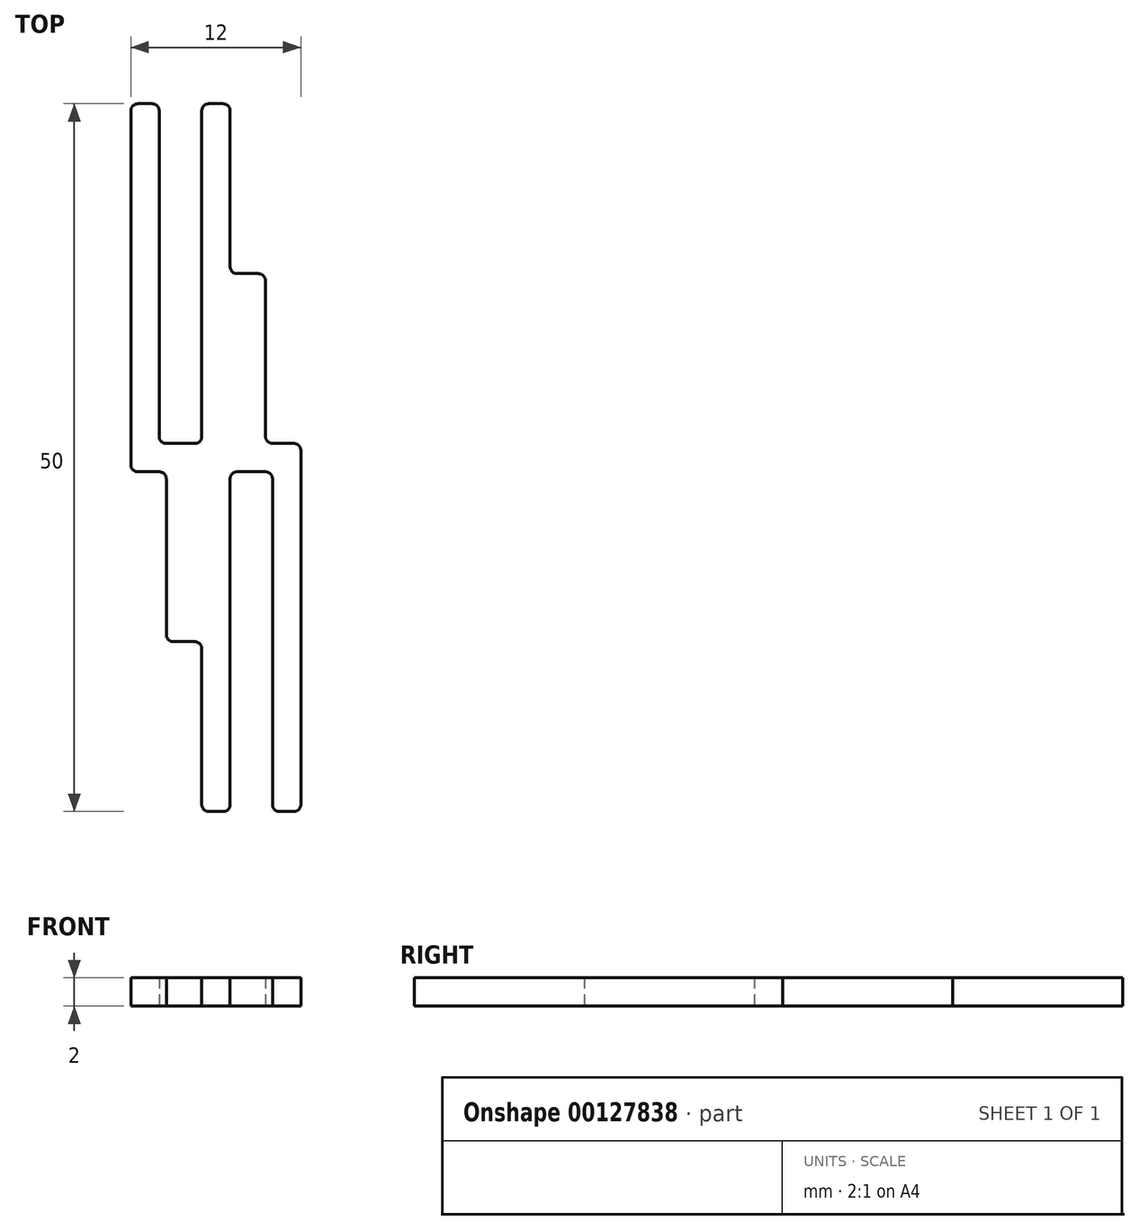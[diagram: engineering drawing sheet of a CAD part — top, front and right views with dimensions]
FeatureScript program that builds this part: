
annotation { "Feature Type Name" : "Feature", "Feature Type Description" : "" }
export const myFeature = defineFeature(function(context is Context, id is Id, definition is map)
    precondition{}
    {
        {
            var Q0;
            Q0=qCreatedBy(makeId("Top.planeOp"),FACE);
            var sketch = newSketch(context, id + "F0", { "sketchPlane" : qUnion([Q0])});
            skLineSegment(sketch, "E0.bottom", {"start": v(-1, -25) * mm, "end": v(1, -25) * mm});
            skLineSegment(sketch, "E0.top", {"start": v(-1, 25) * mm, "end": v(1, 25) * mm});
            skLineSegment(sketch, "E0.left", {"start": v(-1, -25) * mm, "end": v(-1, 25) * mm});
            skLineSegment(sketch, "E0.right", {"start": v(1, -25) * mm, "end": v(1, 25) * mm});
            skPoint(sketch, "E0.middle", {"position": v(0, 0) * mm});
            skLineSegment(sketch, "E1", {"start": v(1, 0) * mm, "end": v(-1, 0) * mm, "construction": true});
            skLineSegment(sketch, "E2", {"start": v(-1, 0) * mm, "end": v(-5, 0) * mm, "construction": true});
            skLineSegment(sketch, "E3", {"start": v(-5, 0) * mm, "end": v(-5, 25) * mm, "construction": true});
            skLineSegment(sketch, "E4.0", {"start": v(-4, 1) * mm, "end": v(-4, 25) * mm});
            skLineSegment(sketch, "E4.1", {"start": v(-1, 1) * mm, "end": v(-4, 1) * mm});
            skLineSegment(sketch, "E5.0", {"start": v(-6, -1) * mm, "end": v(-6, 25) * mm});
            skLineSegment(sketch, "E5.1", {"start": v(-1, -1) * mm, "end": v(-6, -1) * mm});
            skLineSegment(sketch, "E6", {"start": v(-6, 25) * mm, "end": v(-4, 25) * mm});
            skLineSegment(sketch, "E7", {"start": v(1, 0) * mm, "end": v(5, 0) * mm, "construction": true});
            skLineSegment(sketch, "E8", {"start": v(5, 0) * mm, "end": v(5, -25) * mm, "construction": true});
            skLineSegment(sketch, "E9.0", {"start": v(4, -1) * mm, "end": v(4, -25) * mm});
            skLineSegment(sketch, "E9.1", {"start": v(1, -1) * mm, "end": v(4, -1) * mm});
            skLineSegment(sketch, "E10.0", {"start": v(6, 1) * mm, "end": v(6, -25) * mm});
            skLineSegment(sketch, "E10.1", {"start": v(1, 1) * mm, "end": v(6, 1) * mm});
            skLineSegment(sketch, "E11", {"start": v(4, -25) * mm, "end": v(6, -25) * mm});
            skLineSegment(sketch, "E12.bottom", {"start": v(3.5, 1) * mm, "end": v(1, 1) * mm});
            skLineSegment(sketch, "E12.top", {"start": v(3.5, 13) * mm, "end": v(1, 13) * mm});
            skLineSegment(sketch, "E12.left", {"start": v(3.5, 1) * mm, "end": v(3.5, 13) * mm});
            skLineSegment(sketch, "E12.right", {"start": v(1, 1) * mm, "end": v(1, 13) * mm});
            skLineSegment(sketch, "E13.bottom", {"start": v(-3.5, -1) * mm, "end": v(-1, -1) * mm});
            skLineSegment(sketch, "E13.top", {"start": v(-3.5, -13) * mm, "end": v(-1, -13) * mm});
            skLineSegment(sketch, "E13.left", {"start": v(-3.5, -1) * mm, "end": v(-3.5, -13) * mm});
            skLineSegment(sketch, "E13.right", {"start": v(-1, -1) * mm, "end": v(-1, -13) * mm});
            skSolve(sketch);
        }
        {
            var Q0;
            Q0 = qSketchRegion(id + "F0", true);
            extrude(context, id + "F1", {"entities" : qUnion([Q0]), "depth" : 2 * mm});
        }
        {
            var Q0;
            Q0=makeQuery(id+"F1.opExtrude","SWEPT_EDGE",EDGE,{"disambiguationData":[OSD([sQuery(id+"F0.wireOp",EDGE,"E0.bottom"),sQuery(id+"F0.wireOp",EDGE,"E0.left")])]});
            var Q1;
            Q1=makeQuery(id+"F1.opExtrude","SWEPT_EDGE",EDGE,{"disambiguationData":[OSD([sQuery(id+"F0.wireOp",EDGE,"E0.left"),sQuery(id+"F0.wireOp",EDGE,"E5.1")])]});
            var Q2;
            Q2=makeQuery(id+"F1.opExtrude","SWEPT_EDGE",EDGE,{"disambiguationData":[OSD([sQuery(id+"F0.wireOp",EDGE,"E5.0"),sQuery(id+"F0.wireOp",EDGE,"E5.1")])]});
            var Q3;
            Q3=makeQuery(id+"F1.opExtrude","SWEPT_EDGE",EDGE,{"disambiguationData":[OSD([sQuery(id+"F0.wireOp",EDGE,"E0.bottom"),sQuery(id+"F0.wireOp",EDGE,"E0.right")])]});
            var Q4;
            Q4=makeQuery(id+"F1.opExtrude","SWEPT_EDGE",EDGE,{"disambiguationData":[OSD([sQuery(id+"F0.wireOp",EDGE,"E9.0"),sQuery(id+"F0.wireOp",EDGE,"E11")])]});
            var Q5;
            Q5=makeQuery(id+"F1.opExtrude","SWEPT_EDGE",EDGE,{"disambiguationData":[OSD([sQuery(id+"F0.wireOp",EDGE,"E10.0"),sQuery(id+"F0.wireOp",EDGE,"E11")])]});
            var Q6;
            Q6=makeQuery(id+"F1.opExtrude","SWEPT_EDGE",EDGE,{"disambiguationData":[OSD([sQuery(id+"F0.wireOp",EDGE,"E0.right"),sQuery(id+"F0.wireOp",EDGE,"E9.1")])]});
            var Q7;
            Q7=makeQuery(id+"F1.opExtrude","SWEPT_EDGE",EDGE,{"disambiguationData":[OSD([sQuery(id+"F0.wireOp",EDGE,"E9.0"),sQuery(id+"F0.wireOp",EDGE,"E9.1")])]});
            var Q8;
            Q8=makeQuery(id+"F1.opExtrude","SWEPT_EDGE",EDGE,{"disambiguationData":[OSD([sQuery(id+"F0.wireOp",EDGE,"E10.0"),sQuery(id+"F0.wireOp",EDGE,"E10.1")])]});
            var Q9;
            Q9=makeQuery(id+"F1.opExtrude","SWEPT_EDGE",EDGE,{"disambiguationData":[OSD([sQuery(id+"F0.wireOp",EDGE,"E0.right"),sQuery(id+"F0.wireOp",EDGE,"E10.1")])]});
            var Q10;
            Q10=makeQuery(id+"F1.opExtrude","SWEPT_EDGE",EDGE,{"disambiguationData":[OSD([sQuery(id+"F0.wireOp",EDGE,"E4.0"),sQuery(id+"F0.wireOp",EDGE,"E4.1")])]});
            var Q11;
            Q11=makeQuery(id+"F1.opExtrude","SWEPT_EDGE",EDGE,{"disambiguationData":[OSD([sQuery(id+"F0.wireOp",EDGE,"E0.left"),sQuery(id+"F0.wireOp",EDGE,"E4.1")])]});
            var Q12;
            Q12=makeQuery(id+"F1.opExtrude","SWEPT_EDGE",EDGE,{"disambiguationData":[OSD([sQuery(id+"F0.wireOp",EDGE,"E5.0"),sQuery(id+"F0.wireOp",EDGE,"E6")])]});
            var Q13;
            Q13=makeQuery(id+"F1.opExtrude","SWEPT_EDGE",EDGE,{"disambiguationData":[OSD([sQuery(id+"F0.wireOp",EDGE,"E4.0"),sQuery(id+"F0.wireOp",EDGE,"E6")])]});
            var Q14;
            Q14=makeQuery(id+"F1.opExtrude","SWEPT_EDGE",EDGE,{"disambiguationData":[OSD([sQuery(id+"F0.wireOp",EDGE,"E0.top"),sQuery(id+"F0.wireOp",EDGE,"E0.left")])]});
            var Q15;
            Q15=makeQuery(id+"F1.opExtrude","SWEPT_EDGE",EDGE,{"disambiguationData":[OSD([sQuery(id+"F0.wireOp",EDGE,"E0.top"),sQuery(id+"F0.wireOp",EDGE,"E0.right")])]});
            var Q16;
            Q16=makeQuery(id+"F1.opExtrude","SWEPT_EDGE",EDGE,{"disambiguationData":[OSD([sQuery(id+"F0.wireOp",EDGE,"E12.top"),sQuery(id+"F0.wireOp",EDGE,"E12.left")])]});
            var Q17;
            Q17=makeQuery(id+"F1.opExtrude","SWEPT_EDGE",EDGE,{"disambiguationData":[OSD([sQuery(id+"F0.wireOp",EDGE,"E13.top"),sQuery(id+"F0.wireOp",EDGE,"E13.left")])]});
            var Q18;
            Q18=makeQuery(id+"F1.opExtrude","SWEPT_EDGE",EDGE,{"disambiguationData":[OSD([sQuery(id+"F0.wireOp",EDGE,"E5.1"),sQuery(id+"F0.wireOp",EDGE,"E13.bottom"),sQuery(id+"F0.wireOp",EDGE,"E13.left")])]});
            var Q19;
            Q19=makeQuery(id+"F1.opExtrude","SWEPT_EDGE",EDGE,{"disambiguationData":[OSD([sQuery(id+"F0.wireOp",EDGE,"E10.1"),sQuery(id+"F0.wireOp",EDGE,"E12.bottom"),sQuery(id+"F0.wireOp",EDGE,"E12.left")])]});
            var Q20;
            Q20=makeQuery(id+"F1.opExtrude","SWEPT_EDGE",EDGE,{"disambiguationData":[OSD([sQuery(id+"F0.wireOp",EDGE,"E0.left"),sQuery(id+"F0.wireOp",EDGE,"E13.top"),sQuery(id+"F0.wireOp",EDGE,"E13.right")])]});
            var Q21;
            Q21=makeQuery(id+"F1.opExtrude","SWEPT_EDGE",EDGE,{"disambiguationData":[OSD([sQuery(id+"F0.wireOp",EDGE,"E0.right"),sQuery(id+"F0.wireOp",EDGE,"E12.top"),sQuery(id+"F0.wireOp",EDGE,"E12.right")])]});
            fillet(context, id + "F2", {"entities" : qUnion([Q0, Q1, Q2, Q3, Q4, Q5, Q6, Q7, Q8, Q9, Q10, Q11, Q12, Q13, Q14, Q15, Q16, Q17, Q18, Q19, Q20, Q21]), "radius" : .5 * mm, "tangentPropagation" : true, "allowEdgeOverflow" : false});
        }
    });
